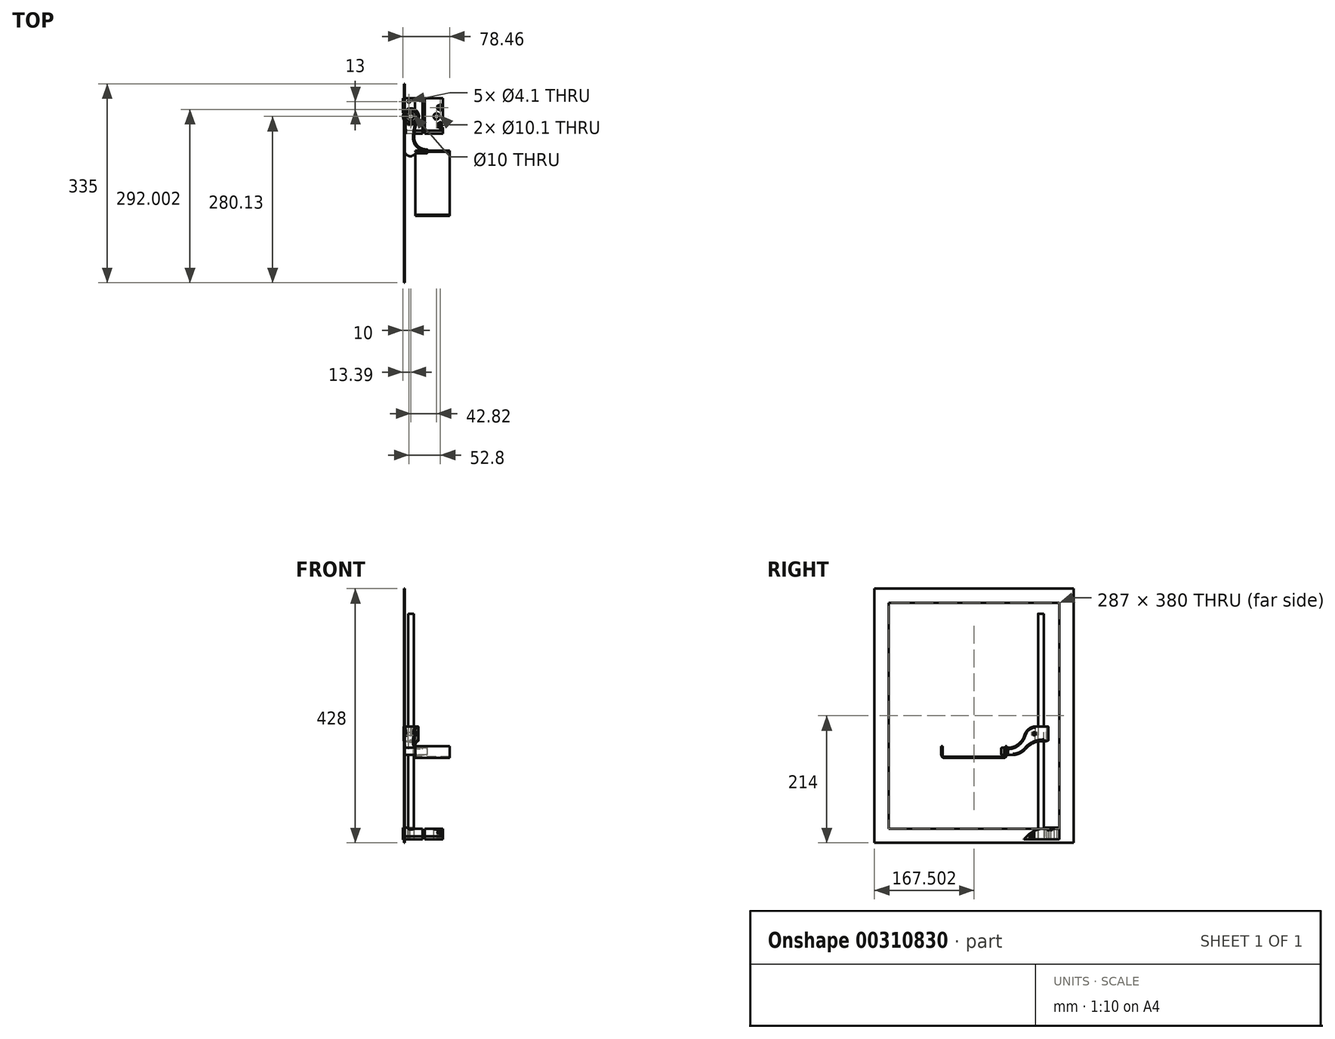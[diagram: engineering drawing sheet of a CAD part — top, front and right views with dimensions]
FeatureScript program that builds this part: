
annotation { "Feature Type Name" : "Feature", "Feature Type Description" : "" }
export const myFeature = defineFeature(function(context is Context, id is Id, definition is map)
    precondition{}
    {
        {
            var Q0;
            Q0=qCreatedBy(makeId("Top.planeOp"),FACE);
            var sketch = newSketch(context, id + "F0", { "sketchPlane" : qUnion([Q0])});
            skLineSegment(sketch, "E0", {"start": v(-50.7, -30.46) * mm, "end": v(-50.7, 5.6) * mm, "construction": true});
            skLineSegment(sketch, "E1", {"start": v(-12.7, -29.55) * mm, "end": v(-12.7, -27.28) * mm});
            skLineSegment(sketch, "E2", {"start": v(-12.7, -27.28) * mm, "end": v(-32.5, -27.28) * mm});
            skLineSegment(sketch, "E3", {"start": v(-32.5, -25.09) * mm, "end": v(-12.7, -25.09) * mm});
            skLineSegment(sketch, "E4", {"start": v(-12.7, -25.09) * mm, "end": v(-12.7, -23) * mm});
            skLineSegment(sketch, "E5", {"start": v(-12.7, -23) * mm, "end": v(-14.49, -23) * mm});
            skLineSegment(sketch, "E6", {"start": v(-34.49, -3) * mm, "end": v(-34.49, -2.73) * mm});
            skLineSegment(sketch, "E7", {"start": v(-32.5, -25.09) * mm, "end": v(-32.5, -27.28) * mm});
            skLineSegment(sketch, "E8", {"start": v(-40, -30.46) * mm, "end": v(-40, 32.54) * mm, "construction": true});
            skArc(sketch, "E9", {"start": v(-41, 41.99) * mm, "mid": v(-40, 23.04) * mm, "end": v(-39, 41.99) * mm});
            skArc(sketch, "E10", {"start": v(-28.44, 27.77) * mm, "mid": v(-29.34, 39.07) * mm, "end": v(-39, 45) * mm});
            skPoint(sketch, "E11.visualSharp", {"position": v(-50.7, 26.08) * mm});
            skArc(sketch, "E11.filletArc", {"start": v(-50.7, 5.6) * mm, "mid": v(-51.12, 18.27) * mm, "end": v(-52.39, 30.88) * mm});
            skPoint(sketch, "E12.visualSharp", {"position": v(-34.49, -23) * mm});
            skArc(sketch, "E12.filletArc", {"start": v(-34.49, -3) * mm, "mid": v(-28.63, -17.14) * mm, "end": v(-14.49, -23) * mm});
            skPoint(sketch, "E13.visualSharp", {"position": v(-34.49, 21.32) * mm});
            skArc(sketch, "E13.filletArc", {"start": v(-28.44, 27.77) * mm, "mid": v(-32.96, 12.82) * mm, "end": v(-34.49, -2.73) * mm});
            skLineSegment(sketch, "E14", {"start": v(-50.7, -24.74) * mm, "end": v(-50.7, 5.6) * mm});
            skLineSegment(sketch, "E15", {"start": v(-29.97, -29.55) * mm, "end": v(-12.7, -29.55) * mm});
            skPoint(sketch, "E16.visualSharp", {"position": v(-50.7, -40.46) * mm});
            skPoint(sketch, "E17.newPointA", {"position": v(-32.5, -24.6) * mm});
            skLineSegment(sketch, "E18.bottom", {"start": v(-39, 40.44) * mm, "end": v(-41, 40.44) * mm, "construction": true});
            skLineSegment(sketch, "E18.top", {"start": v(-39, 48.56) * mm, "end": v(-41, 48.56) * mm, "construction": true});
            skLineSegment(sketch, "E18.left", {"start": v(-39, 40.44) * mm, "end": v(-39, 48.56) * mm, "construction": true});
            skLineSegment(sketch, "E18.right", {"start": v(-41, 40.44) * mm, "end": v(-41, 48.56) * mm, "construction": true});
            skPoint(sketch, "E18.middle", {"position": v(-40, 44.5) * mm});
            skLineSegment(sketch, "E19", {"start": v(-41, 45) * mm, "end": v(-41, 41.99) * mm});
            skPoint(sketch, "E19.endSnap0", {"position": v(-41, 44.5) * mm});
            skLineSegment(sketch, "E20", {"start": v(-39, 45) * mm, "end": v(-39, 41.99) * mm});
            skArc(sketch, "E21.trimOffspring", {"start": v(-41, 45) * mm, "mid": v(-49.73, 40.39) * mm, "end": v(-52.39, 30.88) * mm});
            skLineSegment(sketch, "E22", {"start": v(0, -74.8) * mm, "end": v(0, 75.26) * mm, "construction": true});
            skArc(sketch, "E23.MirrorCS", {"start": v(41, 45) * mm, "mid": v(49.73, 40.39) * mm, "end": v(52.39, 30.88) * mm});
            skLineSegment(sketch, "E24.MirrorCS", {"start": v(41, 45) * mm, "end": v(41, 41.99) * mm});
            skArc(sketch, "E25.MirrorCS", {"start": v(50.7, 5.6) * mm, "mid": v(51.12, 18.27) * mm, "end": v(52.39, 30.88) * mm});
            skLineSegment(sketch, "E26.MirrorCS", {"start": v(12.7, -27.28) * mm, "end": v(32.5, -27.28) * mm});
            skPoint(sketch, "E27.MirrorP", {"position": v(41, 44.5) * mm});
            skLineSegment(sketch, "E28.MirrorCS", {"start": v(34.49, -3) * mm, "end": v(34.49, -2.73) * mm});
            skPoint(sketch, "E29.MirrorP", {"position": v(32.5, -24.6) * mm});
            skPoint(sketch, "E30.MirrorP", {"position": v(50.7, -40.46) * mm});
            skLineSegment(sketch, "E31.MirrorCS", {"start": v(32.5, -29.55) * mm, "end": v(12.7, -29.55) * mm});
            skLineSegment(sketch, "E32.MirrorCS", {"start": v(39, 48.56) * mm, "end": v(41, 48.56) * mm, "construction": true});
            skPoint(sketch, "E33.MirrorP", {"position": v(34.49, -23) * mm});
            skLineSegment(sketch, "E34.MirrorCS", {"start": v(32.5, -25.09) * mm, "end": v(12.7, -25.09) * mm});
            skPoint(sketch, "E35.MirrorP", {"position": v(50.7, 26.08) * mm});
            skLineSegment(sketch, "E36.MirrorCS", {"start": v(32.5, -25.09) * mm, "end": v(32.5, -27.28) * mm});
            skLineSegment(sketch, "E37.MirrorCS", {"start": v(39, 45) * mm, "end": v(39, 41.99) * mm});
            skLineSegment(sketch, "E38.MirrorCS", {"start": v(41, 40.44) * mm, "end": v(41, 48.56) * mm, "construction": true});
            skLineSegment(sketch, "E39.MirrorCS", {"start": v(12.7, -25.09) * mm, "end": v(12.7, -23) * mm});
            skLineSegment(sketch, "E40.MirrorCS", {"start": v(40, -30.46) * mm, "end": v(40, 32.54) * mm, "construction": true});
            skLineSegment(sketch, "E41.MirrorCS", {"start": v(12.7, -29.55) * mm, "end": v(33.16, -29.55) * mm, "construction": true});
            skPoint(sketch, "E42.MirrorP", {"position": v(40, 44.5) * mm});
            skLineSegment(sketch, "E43.MirrorCS", {"start": v(12.7, -23) * mm, "end": v(14.49, -23) * mm});
            skPoint(sketch, "E44.MirrorP", {"position": v(34.49, 21.32) * mm});
            skArc(sketch, "E45.MirrorCS", {"start": v(41, 41.99) * mm, "mid": v(40, 23.04) * mm, "end": v(39, 41.99) * mm});
            skLineSegment(sketch, "E46.MirrorCS", {"start": v(50.7, -30.46) * mm, "end": v(50.7, 5.6) * mm, "construction": true});
            skArc(sketch, "E47.MirrorCS", {"start": v(34.49, -3) * mm, "mid": v(28.63, -17.14) * mm, "end": v(14.49, -23) * mm});
            skLineSegment(sketch, "E48.MirrorCS", {"start": v(39, 40.44) * mm, "end": v(39, 48.56) * mm, "construction": true});
            skLineSegment(sketch, "E49.MirrorCS", {"start": v(39, 40.44) * mm, "end": v(41, 40.44) * mm, "construction": true});
            skLineSegment(sketch, "E50.MirrorCS", {"start": v(50.7, -24.74) * mm, "end": v(50.7, 5.6) * mm});
            skArc(sketch, "E51.MirrorCS", {"start": v(28.44, 27.77) * mm, "mid": v(29.34, 39.07) * mm, "end": v(39, 45) * mm});
            skLineSegment(sketch, "E52.MirrorCS", {"start": v(12.7, -29.55) * mm, "end": v(12.7, -27.28) * mm});
            skArc(sketch, "E53.MirrorCS", {"start": v(28.44, 27.77) * mm, "mid": v(32.96, 12.82) * mm, "end": v(34.49, -2.73) * mm});
            skArc(sketch, "E54", {"start": v(-50.7, -24.74) * mm, "mid": v(-44.43, -33.83) * mm, "end": v(-33.7, -31.22) * mm});
            skPoint(sketch, "E55.visualSharp", {"position": v(-32.5, -29.55) * mm});
            skArc(sketch, "E55.filletArc", {"start": v(-29.97, -29.55) * mm, "mid": v(-32.01, -29.98) * mm, "end": v(-33.7, -31.22) * mm});
            skArc(sketch, "E56.MirrorCS", {"start": v(50.7, -24.74) * mm, "mid": v(44.43, -33.83) * mm, "end": v(33.7, -31.22) * mm});
            skArc(sketch, "E57.MirrorCS", {"start": v(29.97, -29.55) * mm, "mid": v(32.01, -29.98) * mm, "end": v(33.7, -31.22) * mm});
            skLineSegment(sketch, "E58", {"start": v(-59.42, -34.47) * mm, "end": v(64.51, -34.47) * mm, "construction": true});
            skSolve(sketch);
        }
        {
            var Q0;
            Q0=makeQuery(id+"F0.imprint","IMPRINT",FACE,{"disambiguationData":[TD([[makeQuery(id+"F0.imprint","IMPRINT",EDGE,{"derivedFrom":sQuery(id+"F0.wireOp",EDGE,"E1")}),1.0]])]});
            var Q1;
            Q1=makeQuery(id+"F0.imprint","IMPRINT",FACE,{"disambiguationData":[TD([[makeQuery(id+"F0.imprint","IMPRINT",EDGE,{"derivedFrom":sQuery(id+"F0.wireOp",EDGE,"E23.MirrorCS")}),-1.0]])]});
            extrude(context, id + "F1", {"entities" : qUnion([Q0, Q1]), "depth" : 48 * mm});
        }
        {
            var Q0;
            Q0=qCreatedBy(makeId("Right.planeOp"),FACE);
            var sketch = newSketch(context, id + "F2", { "sketchPlane" : qUnion([Q0])});
            skLineSegment(sketch, "E59", {"start": v(-34.5, 0) * mm, "end": v(-34.5, 48) * mm, "construction": true});
            skLineSegment(sketch, "E60", {"start": v(45, 0) * mm, "end": v(45, 48) * mm, "construction": true});
            skLineSegment(sketch, "E61", {"start": v(45, 24) * mm, "end": v(-34.5, 24) * mm, "construction": true});
            skLineSegment(sketch, "E62", {"start": v(20, 0) * mm, "end": v(20, 48) * mm, "construction": true});
            skLineSegment(sketch, "E63", {"start": v(-34.5, 0) * mm, "end": v(-15.8, 0) * mm});
            skLineSegment(sketch, "E64", {"start": v(5.86, 9.24) * mm, "end": v(8.19, 11.67) * mm});
            skLineSegment(sketch, "E65", {"start": v(37.07, 24) * mm, "end": v(45, 24) * mm});
            skPoint(sketch, "E66.visualSharp", {"position": v(20, 24) * mm});
            skArc(sketch, "E66.filletArc", {"start": v(37.07, 24) * mm, "mid": v(21.37, 20.79) * mm, "end": v(8.19, 11.67) * mm});
            skPoint(sketch, "E67.visualSharp", {"position": v(-3, 0) * mm});
            skArc(sketch, "E67.filletArc", {"start": v(-15.8, 0) * mm, "mid": v(-4.03, 2.4) * mm, "end": v(5.86, 9.24) * mm});
            skLineSegment(sketch, "E68", {"start": v(45, 48) * mm, "end": v(24.14, 48) * mm});
            skLineSegment(sketch, "E69", {"start": v(5.28, 34.67) * mm, "end": v(4.34, 32) * mm});
            skLineSegment(sketch, "E70", {"start": v(-23.94, 12) * mm, "end": v(-34.5, 12) * mm});
            skPoint(sketch, "E71.visualSharp", {"position": v(10, 48) * mm});
            skArc(sketch, "E71.filletArc", {"start": v(24.14, 48) * mm, "mid": v(12.6, 44.33) * mm, "end": v(5.28, 34.67) * mm});
            skPoint(sketch, "E72.visualSharp", {"position": v(-2.73, 12) * mm});
            skArc(sketch, "E72.filletArc", {"start": v(-23.94, 12) * mm, "mid": v(-6.63, 17.5) * mm, "end": v(4.34, 32) * mm});
            skLineSegment(sketch, "E73", {"start": v(24.14, 48) * mm, "end": v(-34.5, 48) * mm});
            skLineSegment(sketch, "E74", {"start": v(-34.5, 48) * mm, "end": v(-34.5, 12) * mm});
            skLineSegment(sketch, "E75", {"start": v(45, 24) * mm, "end": v(45, 0) * mm});
            skLineSegment(sketch, "E76", {"start": v(45, 0) * mm, "end": v(-15.8, 0) * mm});
            skSolve(sketch);
        }
        {
            var Q0;
            Q0 = qSketchRegion(id + "F2", true);
            extrude(context, id + "F3", {"entities" : qUnion([Q0]), "operationType" : NewBodyOperationType.REMOVE, "endBound" : BoundingType.THROUGH_ALL, "oppositeDirection" : true, "depth" : 25 * mm, "hasSecondDirection" : true, "secondDirectionBound" : BoundingType.THROUGH_ALL, "secondDirectionOppositeDirection" : false, "secondDirectionDepth" : 25 * mm});
        }
        {
            var Q0;
            Q0=makeQuery(id+"F3.boolean.opBoolean","INTERSECT",EDGE,{"derivedFrom":[makeQuery(id+"F1.opExtrude","SWEPT_FACE",FACE,{"disambiguationData":[OSD([sQuery(id+"F0.wireOp",EDGE,"E56.MirrorCS")])]}),makeQuery(id+"F3.opExtrude","SWEPT_FACE",FACE,{"disambiguationData":[OSD([sQuery(id+"F2.wireOp",EDGE,"E70")])]})]});
            var Q1;
            Q1=makeQuery(id+"F3.boolean.opBoolean","INTERSECT",EDGE,{"derivedFrom":[makeQuery(id+"F1.opExtrude","SWEPT_FACE",FACE,{"disambiguationData":[OSD([sQuery(id+"F0.wireOp",EDGE,"E50.MirrorCS")])]}),makeQuery(id+"F3.opExtrude","SWEPT_FACE",FACE,{"disambiguationData":[OSD([sQuery(id+"F2.wireOp",EDGE,"E67.filletArc")])]})]});
            var Q2;
            Q2=makeQuery(id+"F3.boolean.opBoolean","INTERSECT",EDGE,{"derivedFrom":[makeQuery(id+"F1.opExtrude","SWEPT_FACE",FACE,{"disambiguationData":[OSD([sQuery(id+"F0.wireOp",EDGE,"E14")])]}),makeQuery(id+"F3.opExtrude","SWEPT_FACE",FACE,{"disambiguationData":[OSD([sQuery(id+"F2.wireOp",EDGE,"E72.filletArc")])]})]});
            var Q3;
            Q3=makeQuery(id+"F3.boolean.opBoolean","INTERSECT",EDGE,{"derivedFrom":[makeQuery(id+"F1.opExtrude","SWEPT_FACE",FACE,{"disambiguationData":[OSD([sQuery(id+"F0.wireOp",EDGE,"E14")])]}),makeQuery(id+"F3.opExtrude","SWEPT_FACE",FACE,{"disambiguationData":[OSD([sQuery(id+"F2.wireOp",EDGE,"E67.filletArc")])]})]});
            var Q4;
            Q4=makeQuery(id+"F3.boolean.opBoolean","INTERSECT",EDGE,{"derivedFrom":[makeQuery(id+"F1.opExtrude","SWEPT_FACE",FACE,{"disambiguationData":[OSD([sQuery(id+"F0.wireOp",EDGE,"E53.MirrorCS")])]}),makeQuery(id+"F3.opExtrude","SWEPT_FACE",FACE,{"disambiguationData":[OSD([sQuery(id+"F2.wireOp",EDGE,"E71.filletArc")])]})]});
            var Q5;
            Q5=makeQuery(id+"F3.boolean.opBoolean","INTERSECT",EDGE,{"derivedFrom":[makeQuery(id+"F1.opExtrude","SWEPT_FACE",FACE,{"disambiguationData":[OSD([sQuery(id+"F0.wireOp",EDGE,"E13.filletArc")])]}),makeQuery(id+"F3.opExtrude","SWEPT_FACE",FACE,{"disambiguationData":[OSD([sQuery(id+"F2.wireOp",EDGE,"E71.filletArc")])]})]});
            var Q6;
            Q6=makeQuery(id+"F3.boolean.opBoolean","INTERSECT",EDGE,{"derivedFrom":[makeQuery(id+"F1.opExtrude","SWEPT_FACE",FACE,{"disambiguationData":[OSD([sQuery(id+"F0.wireOp",EDGE,"E13.filletArc")])]}),makeQuery(id+"F3.opExtrude","SWEPT_FACE",FACE,{"disambiguationData":[OSD([sQuery(id+"F2.wireOp",EDGE,"E66.filletArc")])]})]});
            var Q7;
            Q7=makeQuery(id+"F3.boolean.opBoolean","INTERSECT",EDGE,{"derivedFrom":[makeQuery(id+"F1.opExtrude","SWEPT_FACE",FACE,{"disambiguationData":[OSD([sQuery(id+"F0.wireOp",EDGE,"E53.MirrorCS")])]}),makeQuery(id+"F3.opExtrude","SWEPT_FACE",FACE,{"disambiguationData":[OSD([sQuery(id+"F2.wireOp",EDGE,"E66.filletArc")])]})]});
            fillet(context, id + "F4", {"entities" : qUnion([Q0, Q1, Q2, Q3, Q4, Q5, Q6, Q7]), "radius" : 2 * mm, "tangentPropagation" : true, "rho" : .8, "crossSection" : FilletCrossSection.CONIC, "allowEdgeOverflow" : false});
        }
        {
            var Q0;
            Q0=qCreatedBy(makeId("Right.planeOp"),FACE);
            var Q1;
            Q1=sQuery(id+"F0.wireOp",VERTEX,"E10.center");
            cPlane(context, id + "F5", {"entities" : qUnion([Q0, Q1]), "cplaneType" : CPlaneType.PLANE_POINT, "offset" : 25 * mm, "width" : 150 * mm, "height" : 150 * mm});
        }
        {
            var Q0;
            Q0=qCreatedBy(id+"F5.planeOp",FACE);
            var sketch = newSketch(context, id + "F6", { "sketchPlane" : qUnion([Q0])});
            skLineSegment(sketch, "E77", {"start": v(45, 0) * mm, "end": v(45, 48) * mm, "construction": true});
            skLineSegment(sketch, "E78", {"start": v(42, 0) * mm, "end": v(42, 48) * mm, "construction": true});
            skLineSegment(sketch, "E79", {"start": v(32.5, 0) * mm, "end": v(32.5, 48) * mm, "construction": true});
            skLineSegment(sketch, "E80.MirrorCS", {"start": v(23, 0) * mm, "end": v(23, 48) * mm, "construction": true});
            skLineSegment(sketch, "E81.MirrorCS", {"start": v(20, 0) * mm, "end": v(20, 48) * mm, "construction": true});
            skLineSegment(sketch, "E82", {"start": v(45, 24) * mm, "end": v(20, 24) * mm, "construction": true});
            skLineSegment(sketch, "E83", {"start": v(20, 48) * mm, "end": v(45, 48) * mm, "construction": true});
            skLineSegment(sketch, "E84", {"start": v(45, 48) * mm, "end": v(45, 24) * mm, "construction": true});
            skLineSegment(sketch, "E85", {"start": v(45, 36) * mm, "end": v(18, 36) * mm, "construction": true});
            skLineSegment(sketch, "E86.bottom", {"start": v(17, 33.5) * mm, "end": v(19, 33.5) * mm});
            skLineSegment(sketch, "E86.top", {"start": v(17, 38.5) * mm, "end": v(19, 38.5) * mm});
            skLineSegment(sketch, "E86.left", {"start": v(17, 33.5) * mm, "end": v(17, 38.5) * mm});
            skLineSegment(sketch, "E86.right", {"start": v(19, 33.5) * mm, "end": v(19, 38.5) * mm});
            skPoint(sketch, "E86.middle", {"position": v(18, 36) * mm});
            skSolve(sketch);
        }
        {
            var Q0;
            Q0 = qSketchRegion(id + "F6", true);
            var Q1;
            Q1=sQuery(id+"F6.wireOp",EDGE,"E79");
            revolve(context, id + "F7", {"entities" : qUnion([Q0]), "axis" : qUnion([Q1]), "revolveType" : RevolveType.FULL, "oppositeDirection" : true});
        }
        {
            var Q0;
            Q0=makeQuery(id+"F7.opRevolve","SWEPT_BODY",BODY,{"disambiguationData":[OSD([sQuery(id+"F6.wireOp",EDGE,"E86.bottom"),sQuery(id+"F6.wireOp",EDGE,"E86.top"),sQuery(id+"F6.wireOp",EDGE,"E86.left"),sQuery(id+"F6.wireOp",EDGE,"E86.right")])]});
            var Q1;
            Q1=qCreatedBy(makeId("Right.planeOp"),FACE);
            mirror(context, id + "F8", {"entities" : qUnion([Q0]), "mirrorPlane" : qUnion([Q1])});
        }
        {
            var Q0;
            Q0=makeQuery(id+"F7.opRevolve","SWEPT_BODY",BODY,{"disambiguationData":[OSD([sQuery(id+"F6.wireOp",EDGE,"E86.bottom"),sQuery(id+"F6.wireOp",EDGE,"E86.top"),sQuery(id+"F6.wireOp",EDGE,"E86.left"),sQuery(id+"F6.wireOp",EDGE,"E86.right")])]});
            var Q1;
            Q1=makeQuery(id+"F8.opPattern","COPY",BODY,{"derivedFrom":makeQuery(id+"F7.opRevolve","SWEPT_BODY",BODY,{"disambiguationData":[OSD([sQuery(id+"F6.wireOp",EDGE,"E86.bottom"),sQuery(id+"F6.wireOp",EDGE,"E86.top"),sQuery(id+"F6.wireOp",EDGE,"E86.left"),sQuery(id+"F6.wireOp",EDGE,"E86.right")])]}),"instanceName":"1"});
            var Q2;
            Q2=makeQuery(id+"F1.opExtrude","SWEPT_BODY",BODY,{"disambiguationData":[OSD([sQuery(id+"F0.wireOp",EDGE,"E1"),sQuery(id+"F0.wireOp",EDGE,"E2"),sQuery(id+"F0.wireOp",EDGE,"E3"),sQuery(id+"F0.wireOp",EDGE,"E4"),sQuery(id+"F0.wireOp",EDGE,"E5"),sQuery(id+"F0.wireOp",EDGE,"E6"),sQuery(id+"F0.wireOp",EDGE,"E7"),sQuery(id+"F0.wireOp",EDGE,"E9"),sQuery(id+"F0.wireOp",EDGE,"E10"),sQuery(id+"F0.wireOp",EDGE,"E11.filletArc"),sQuery(id+"F0.wireOp",EDGE,"E12.filletArc"),sQuery(id+"F0.wireOp",EDGE,"E13.filletArc"),sQuery(id+"F0.wireOp",EDGE,"E14"),sQuery(id+"F0.wireOp",EDGE,"E15"),sQuery(id+"F0.wireOp",EDGE,"E19"),sQuery(id+"F0.wireOp",EDGE,"E20"),sQuery(id+"F0.wireOp",EDGE,"E21.trimOffspring"),sQuery(id+"F0.wireOp",EDGE,"E54"),sQuery(id+"F0.wireOp",EDGE,"E55.filletArc")])]});
            var Q3;
            Q3=makeQuery(id+"F1.opExtrude","SWEPT_BODY",BODY,{"disambiguationData":[OSD([sQuery(id+"F0.wireOp",EDGE,"E23.MirrorCS"),sQuery(id+"F0.wireOp",EDGE,"E24.MirrorCS"),sQuery(id+"F0.wireOp",EDGE,"E25.MirrorCS"),sQuery(id+"F0.wireOp",EDGE,"E26.MirrorCS"),sQuery(id+"F0.wireOp",EDGE,"E28.MirrorCS"),sQuery(id+"F0.wireOp",EDGE,"E31.MirrorCS"),sQuery(id+"F0.wireOp",EDGE,"E34.MirrorCS"),sQuery(id+"F0.wireOp",EDGE,"E36.MirrorCS"),sQuery(id+"F0.wireOp",EDGE,"E37.MirrorCS"),sQuery(id+"F0.wireOp",EDGE,"E39.MirrorCS"),sQuery(id+"F0.wireOp",EDGE,"E43.MirrorCS"),sQuery(id+"F0.wireOp",EDGE,"E45.MirrorCS"),sQuery(id+"F0.wireOp",EDGE,"E47.MirrorCS"),sQuery(id+"F0.wireOp",EDGE,"E50.MirrorCS"),sQuery(id+"F0.wireOp",EDGE,"E51.MirrorCS"),sQuery(id+"F0.wireOp",EDGE,"E52.MirrorCS"),sQuery(id+"F0.wireOp",EDGE,"E53.MirrorCS"),sQuery(id+"F0.wireOp",EDGE,"E56.MirrorCS"),sQuery(id+"F0.wireOp",EDGE,"E57.MirrorCS")])]});
            booleanBodies(context, id + "F9", {"operationType" : BooleanOperationType.SUBTRACTION, "tools" : qUnion([Q0, Q1]), "targets" : qUnion([Q2, Q3])});
        }
        {
            var Q0;
            Q0=makeQuery(id+"F1.opExtrude","SWEPT_FACE",FACE,{"disambiguationData":[OSD([sQuery(id+"F0.wireOp",EDGE,"E7")])]});
            var sketch = newSketch(context, id + "F10", { "sketchPlane" : qUnion([Q0])});
            skLineSegment(sketch, "E87.bottom", {"start": v(-25.09, 15) * mm, "end": v(-135.09, 15) * mm, "construction": true});
            skLineSegment(sketch, "E87.top", {"start": v(-30.09, -5) * mm, "end": v(-130.09, -5) * mm});
            skLineSegment(sketch, "E87.left", {"start": v(-25.09, 15) * mm, "end": v(-25.09, 0) * mm});
            skLineSegment(sketch, "E87.right", {"start": v(-135.09, 15) * mm, "end": v(-135.09, 0) * mm});
            skPoint(sketch, "E88.visualSharp", {"position": v(-25.09, -5) * mm});
            skArc(sketch, "E88.filletArc", {"start": v(-30.09, -5) * mm, "mid": v(-26.55, -3.54) * mm, "end": v(-25.09, 0) * mm});
            skPoint(sketch, "E89.visualSharp", {"position": v(-135.09, -5) * mm});
            skArc(sketch, "E89.filletArc", {"start": v(-135.09, 0) * mm, "mid": v(-133.62, -3.54) * mm, "end": v(-130.09, -5) * mm});
            skLineSegment(sketch, "E90.0", {"start": v(-133.09, 15) * mm, "end": v(-133.09, 0) * mm});
            skLineSegment(sketch, "E90.1", {"start": v(-27.09, 15) * mm, "end": v(-27.09, 0) * mm});
            skArc(sketch, "E90.2", {"start": v(-30.09, -3) * mm, "mid": v(-27.97, -2.12) * mm, "end": v(-27.09, 0) * mm});
            skLineSegment(sketch, "E90.3", {"start": v(-30.09, -3) * mm, "end": v(-130.09, -3) * mm});
            skArc(sketch, "E90.4", {"start": v(-133.09, 0) * mm, "mid": v(-132.2, -2.12) * mm, "end": v(-130.09, -3) * mm});
            skLineSegment(sketch, "E91", {"start": v(-25.09, 15) * mm, "end": v(-27.09, 15) * mm});
            skLineSegment(sketch, "E92", {"start": v(-133.09, 15) * mm, "end": v(-135.09, 15) * mm});
            skSolve(sketch);
        }
        {
            var Q0;
            Q0 = qSketchRegion(id + "F10", true);
            extrude(context, id + "F11", {"entities" : qUnion([Q0]), "depth" : 57.57 * mm});
        }
        {
            var Q0;
            Q0=qCreatedBy(makeId("Top.planeOp"),FACE);
            var Q1;
            Q1=makeQuery(id+"F1.opExtrude","CAP_VERTEX",VERTEX,{"disambiguationData":[OSD([sQuery(id+"F0.wireOp",EDGE,"E9"),sQuery(id+"F0.wireOp",EDGE,"E19")])],"isStart":false});
            cPlane(context, id + "F12", {"entities" : qUnion([Q0, Q1]), "cplaneType" : CPlaneType.PLANE_POINT, "offset" : 25 * mm, "width" : 150 * mm, "height" : 150 * mm});
        }
        {
            var Q0;
            Q0=qCreatedBy(id+"F12.planeOp",FACE);
            var sketch = newSketch(context, id + "F13", { "sketchPlane" : qUnion([Q0])});
            skCircle(sketch, "E93", {"center": v(-40, 32.54) * mm, "radius": 9.5 * mm});
            skCircle(sketch, "E94", {"center": v(-40, 32.54) * mm, "radius": 5 * mm});
            skSolve(sketch);
        }
        {
            var Q0;
            Q0 = qSketchRegion(id + "F13", true);
            extrude(context, id + "F14", {"entities" : qUnion([Q0]), "oppositeDirection" : true, "depth" : 25 * mm});
        }
        {
            var Q0;
            Q0=makeQuery(id+"F14.opExtrude","CAP_FACE",FACE,{"disambiguationData":[OSD([sQuery(id+"F13.wireOp",EDGE,"E93"),sQuery(id+"F13.wireOp",EDGE,"E94")])],"isStart":true});
            var sketch = newSketch(context, id + "F15", { "sketchPlane" : qUnion([Q0])});
            skCircle(sketch, "E95", {"center": v(-40, 32.54) * mm, "radius": 5 * mm});
            skSolve(sketch);
        }
        {
            var Q0;
            Q0 = qSketchRegion(id + "F15", true);
            extrude(context, id + "F16", {"entities" : qUnion([Q0]), "depth" : 190 * mm, "hasSecondDirection" : true, "secondDirectionOppositeDirection" : true, "secondDirectionDepth" : 190 * mm});
        }
        {
            var Q0;
            Q0=makeQuery(id+"F16.opExtrude","CAP_FACE",FACE,{"disambiguationData":[OSD([sQuery(id+"F15.wireOp",EDGE,"E95")])],"isStart":true});
            var sketch = newSketch(context, id + "F17", { "sketchPlane" : qUnion([Q0])});
            skCircle(sketch, "E96", {"center": v(-40, -32.54) * mm, "radius": 5.05 * mm});
            skLineSegment(sketch, "E97.bottom", {"start": v(-50.6, -63.41) * mm, "end": v(-20.6, -63.41) * mm});
            skLineSegment(sketch, "E97.top", {"start": v(-50.6, -1.67) * mm, "end": v(-20.6, -1.67) * mm});
            skLineSegment(sketch, "E97.left", {"start": v(-50.59, -63.41) * mm, "end": v(-50.6, -1.67) * mm});
            skLineSegment(sketch, "E97.right", {"start": v(-20.6, -63.41) * mm, "end": v(-20.6, -1.67) * mm});
            skPoint(sketch, "E97.middle", {"position": v(-35.6, -32.54) * mm});
            skLineSegment(sketch, "E98", {"start": v(-40, -1.67) * mm, "end": v(-40, -63.41) * mm, "construction": true});
            skSolve(sketch);
        }
        {
            var Q0;
            Q0 = qSketchRegion(id + "F17", true);
            extrude(context, id + "F18", {"entities" : qUnion([Q0]), "oppositeDirection" : true, "depth" : 18 * mm});
        }
        {
            var Q0;
            Q0=makeQuery(id+"F18.opExtrude","SWEPT_FACE",FACE,{"disambiguationData":[OSD([sQuery(id+"F17.wireOp",EDGE,"E97.left")])]});
            var sketch = newSketch(context, id + "F19", { "sketchPlane" : qUnion([Q0])});
            skLineSegment(sketch, "E99.bottom", {"start": v(-63.41, -124) * mm, "end": v(223.59, -124) * mm});
            skLineSegment(sketch, "E99.top", {"start": v(-63.41, 256) * mm, "end": v(223.59, 256) * mm});
            skLineSegment(sketch, "E99.left", {"start": v(-63.41, -124) * mm, "end": v(-63.41, 256) * mm});
            skLineSegment(sketch, "E99.right", {"start": v(223.59, -124) * mm, "end": v(223.59, 256) * mm});
            skLineSegment(sketch, "E100", {"start": v(80.09, 256) * mm, "end": v(80.09, -124) * mm, "construction": true});
            skLineSegment(sketch, "E101", {"start": v(30.09, -5) * mm, "end": v(130.09, -5) * mm, "construction": true});
            skPoint(sketch, "E102", {"position": v(80.09, -5) * mm});
            skLineSegment(sketch, "E103.0", {"start": v(-87.41, -148) * mm, "end": v(-87.41, 280) * mm});
            skLineSegment(sketch, "E103.1", {"start": v(-87.41, -148) * mm, "end": v(247.59, -148) * mm});
            skLineSegment(sketch, "E103.2", {"start": v(247.59, -148) * mm, "end": v(247.59, 280) * mm});
            skLineSegment(sketch, "E103.3", {"start": v(-87.41, 280) * mm, "end": v(247.59, 280) * mm});
            skSolve(sketch);
        }
        {
            var Q0;
            Q0 = qSketchRegion(id + "F19", true);
            extrude(context, id + "F20", {"entities" : qUnion([Q0]), "depth" : 1.2 * mm});
        }
        {
            var Q0;
            Q0=makeQuery(id+"F18.opExtrude","SWEPT_FACE",FACE,{"disambiguationData":[OSD([sQuery(id+"F17.wireOp",EDGE,"E97.right")])]});
            cPlane(context, id + "F21", {"entities" : qUnion([Q0]), "cplaneType" : CPlaneType.OFFSET, "offset" : 2 * mm, "width" : 150 * mm, "height" : 150 * mm});
        }
        {
            var Q0;
            Q0=makeQuery(id+"F18.opExtrude","SWEPT_BODY",BODY,{"disambiguationData":[OSD([sQuery(id+"F17.wireOp",EDGE,"E96"),sQuery(id+"F17.wireOp",EDGE,"E97.bottom"),sQuery(id+"F17.wireOp",EDGE,"E97.top"),sQuery(id+"F17.wireOp",EDGE,"E97.left"),sQuery(id+"F17.wireOp",EDGE,"E97.right")])]});
            var Q1;
            Q1=qCreatedBy(id+"F21.planeOp",FACE);
            mirror(context, id + "F22", {"entities" : qUnion([Q0]), "mirrorPlane" : qUnion([Q1])});
        }
        {
            var Q0;
            Q0=makeQuery(id+"F18.opExtrude","SWEPT_FACE",FACE,{"disambiguationData":[OSD([sQuery(id+"F17.wireOp",EDGE,"E97.left")])]});
            var sketch = newSketch(context, id + "F23", { "sketchPlane" : qUnion([Q0])});
            skLineSegment(sketch, "E104", {"start": v(-44.58, -124) * mm, "end": v(-38.31, -124) * mm});
            skLineSegment(sketch, "E105", {"start": v(-8.57, -137.2) * mm, "end": v(-7.59, -138.4) * mm});
            skLineSegment(sketch, "E106", {"start": v(14.47, -148) * mm, "end": v(34.92, -148) * mm, "construction": true});
            skLineSegment(sketch, "E107", {"start": v(-19.58, -124) * mm, "end": v(-19.58, -148) * mm, "construction": true});
            skPoint(sketch, "E108.visualSharp", {"position": v(-19.58, -124) * mm});
            skArc(sketch, "E108.filletArc", {"start": v(-7.59, -138.4) * mm, "mid": v(-21.35, -127.78) * mm, "end": v(-38.31, -124) * mm});
            skPoint(sketch, "E109.visualSharp", {"position": v(0.42, -148) * mm});
            skArc(sketch, "E109.filletArc", {"start": v(-8.57, -137.2) * mm, "mid": v(1.75, -145.17) * mm, "end": v(14.47, -148) * mm});
            skLineSegment(sketch, "E110", {"start": v(-44.58, -124) * mm, "end": v(14.47, -124) * mm});
            skLineSegment(sketch, "E111", {"start": v(14.47, -124) * mm, "end": v(14.47, -148) * mm});
            skSolve(sketch);
        }
        {
            var Q0;
            Q0 = qSketchRegion(id + "F23", true);
            extrude(context, id + "F24", {"entities" : qUnion([Q0]), "operationType" : NewBodyOperationType.REMOVE, "endBound" : BoundingType.THROUGH_ALL, "oppositeDirection" : true, "depth" : 25 * mm});
        }
        {
            var Q0;
            Q0=makeQuery(id+"F18.opExtrude","SWEPT_FACE",FACE,{"disambiguationData":[OSD([sQuery(id+"F17.wireOp",EDGE,"E97.bottom")])]});
            var sketch = newSketch(context, id + "F25", { "sketchPlane" : qUnion([Q0])});
            skLineSegment(sketch, "E112", {"start": v(52, -124) * mm, "end": v(33.4, -124) * mm});
            skLineSegment(sketch, "E113", {"start": v(33.4, -124) * mm, "end": v(33.4, -122.6) * mm});
            skLineSegment(sketch, "E114", {"start": v(33.4, -122.6) * mm, "end": v(53.4, -122.6) * mm});
            skLineSegment(sketch, "E115", {"start": v(53.4, -122.6) * mm, "end": v(53.4, -142.6) * mm});
            skLineSegment(sketch, "E116", {"start": v(53.4, -142.6) * mm, "end": v(52, -142.6) * mm});
            skLineSegment(sketch, "E117", {"start": v(52, -142.6) * mm, "end": v(52, -124) * mm});
            skSolve(sketch);
        }
        {
            var Q0;
            Q0 = qSketchRegion(id + "F25", true);
            extrude(context, id + "F26", {"entities" : qUnion([Q0]), "oppositeDirection" : true, "depth" : 25 * mm});
        }
        {
            var Q0;
            Q0=makeQuery(id+"F26.opExtrude","SWEPT_FACE",FACE,{"disambiguationData":[OSD([sQuery(id+"F25.wireOp",EDGE,"E114")])]});
            var sketch = newSketch(context, id + "F27", { "sketchPlane" : qUnion([Q0])});
            skLineSegment(sketch, "E118", {"start": v(-43.4, 38.41) * mm, "end": v(-43.4, 63.41) * mm, "construction": true});
            skPoint(sketch, "E119", {"position": v(-43.4, 50.91) * mm});
            skLineSegment(sketch, "E120", {"start": v(-43.4, 44.41) * mm, "end": v(-43.4, 57.41) * mm});
            skCircle(sketch, "E121", {"center": v(-43.4, 44.41) * mm, "radius": 2.05 * mm});
            skCircle(sketch, "E122", {"center": v(-43.4, 57.41) * mm, "radius": 2.05 * mm});
            skSolve(sketch);
        }
        {
            var Q0;
            Q0=makeQuery(id+"F27.imprint","IMPRINT",FACE,{"disambiguationData":[TD([[makeQuery(id+"F27.imprint","IMPRINT",EDGE,{"derivedFrom":sQuery(id+"F27.wireOp",EDGE,"E122")}),1.0]])]});
            var Q1;
            Q1=makeQuery(id+"F27.imprint","IMPRINT",FACE,{"disambiguationData":[TD([[makeQuery(id+"F27.imprint","IMPRINT",EDGE,{"derivedFrom":sQuery(id+"F27.wireOp",EDGE,"E121")}),1.0]])]});
            extrude(context, id + "F28", {"entities" : qUnion([Q0, Q1]), "operationType" : NewBodyOperationType.REMOVE, "oppositeDirection" : true, "depth" : 25 * mm});
        }
        {
            var Q0;
            Q0=makeQuery(id+"F22.opPattern","COPY",FACE,{"derivedFrom":makeQuery(id+"F18.opExtrude","CAP_FACE",FACE,{"disambiguationData":[OSD([sQuery(id+"F17.wireOp",EDGE,"E96"),sQuery(id+"F17.wireOp",EDGE,"E97.bottom"),sQuery(id+"F17.wireOp",EDGE,"E97.top"),sQuery(id+"F17.wireOp",EDGE,"E97.left"),sQuery(id+"F17.wireOp",EDGE,"E97.right")])],"isStart":false}),"instanceName":"1"});
            var sketch = newSketch(context, id + "F29", { "sketchPlane" : qUnion([Q0])});
            skLineSegment(sketch, "E123", {"start": v(9.4, 47.54) * mm, "end": v(9.4, 17.54) * mm, "construction": true});
            skPoint(sketch, "E124", {"position": v(9.4, 32.54) * mm});
            skCircle(sketch, "E125", {"center": v(9.4, 47.54) * mm, "radius": 2.05 * mm});
            skCircle(sketch, "E126", {"center": v(9.4, 17.54) * mm, "radius": 2.05 * mm});
            skCircle(sketch, "E127.cCircle", {"center": v(9.4, 47.54) * mm, "radius": 3.45 * mm, "construction": true});
            skLineSegment(sketch, "E127.0", {"start": v(5.96, 47.05) * mm, "end": v(5.96, 48.03) * mm});
            skLineSegment(sketch, "E127.1", {"start": v(7.26, 50.28) * mm, "end": v(8.11, 50.77) * mm});
            skLineSegment(sketch, "E127.2", {"start": v(10.7, 50.77) * mm, "end": v(11.56, 50.28) * mm});
            skLineSegment(sketch, "E127.3", {"start": v(12.86, 48.03) * mm, "end": v(12.86, 47.05) * mm});
            skLineSegment(sketch, "E127.4", {"start": v(11.56, 44.8) * mm, "end": v(10.7, 44.3) * mm});
            skLineSegment(sketch, "E127.5", {"start": v(8.11, 44.3) * mm, "end": v(7.26, 44.8) * mm});
            skPoint(sketch, "E127.0.midPoint", {"position": v(5.96, 47.54) * mm});
            skArc(sketch, "E128", {"start": v(10.7, 50.77) * mm, "mid": v(9.4, 53.02) * mm, "end": v(8.11, 50.77) * mm});
            skArc(sketch, "E129.1.0", {"start": v(7.26, 50.28) * mm, "mid": v(4.66, 50.28) * mm, "end": v(5.96, 48.03) * mm});
            skArc(sketch, "E129.2.0", {"start": v(5.96, 47.05) * mm, "mid": v(4.66, 44.8) * mm, "end": v(7.26, 44.8) * mm});
            skArc(sketch, "E129.3.0", {"start": v(8.11, 44.3) * mm, "mid": v(9.4, 42.06) * mm, "end": v(10.7, 44.3) * mm});
            skArc(sketch, "E129.4.0", {"start": v(11.56, 44.8) * mm, "mid": v(14.16, 44.8) * mm, "end": v(12.86, 47.05) * mm});
            skArc(sketch, "E129.5.0", {"start": v(12.86, 48.03) * mm, "mid": v(14.16, 50.28) * mm, "end": v(11.56, 50.28) * mm});
            skLineSegment(sketch, "E130", {"start": v(9.4, 32.54) * mm, "end": v(23.54, 32.54) * mm, "construction": true});
            skLineSegment(sketch, "E131.MirrorCS", {"start": v(10.7, 14.3) * mm, "end": v(11.56, 14.8) * mm});
            skLineSegment(sketch, "E132.MirrorCS", {"start": v(7.26, 14.8) * mm, "end": v(8.11, 14.3) * mm});
            skLineSegment(sketch, "E133.MirrorCS", {"start": v(5.96, 18.03) * mm, "end": v(5.96, 17.05) * mm});
            skLineSegment(sketch, "E134.MirrorCS", {"start": v(12.86, 17.05) * mm, "end": v(12.86, 18.03) * mm});
            skCircle(sketch, "E135.MirrorC", {"center": v(9.4, 17.54) * mm, "radius": 3.45 * mm, "construction": true});
            skLineSegment(sketch, "E136.MirrorCS", {"start": v(8.11, 20.77) * mm, "end": v(7.26, 20.28) * mm});
            skLineSegment(sketch, "E137.MirrorCS", {"start": v(11.56, 20.28) * mm, "end": v(10.7, 20.77) * mm});
            skArc(sketch, "E138.MirrorCS", {"start": v(12.86, 17.05) * mm, "mid": v(14.16, 14.8) * mm, "end": v(11.56, 14.8) * mm});
            skPoint(sketch, "E139.MirrorP", {"position": v(5.96, 17.54) * mm});
            skPoint(sketch, "E140.MirrorP", {"position": v(9.4, 21.52) * mm});
            skArc(sketch, "E141.MirrorCS", {"start": v(10.7, 14.3) * mm, "mid": v(9.4, 12.06) * mm, "end": v(8.11, 14.3) * mm});
            skArc(sketch, "E142.MirrorCS", {"start": v(11.56, 20.28) * mm, "mid": v(14.16, 20.28) * mm, "end": v(12.86, 18.03) * mm});
            skArc(sketch, "E143.MirrorCS", {"start": v(5.96, 18.03) * mm, "mid": v(4.66, 20.28) * mm, "end": v(7.26, 20.28) * mm});
            skPoint(sketch, "E144.MirrorP", {"position": v(5.96, 15.55) * mm});
            skArc(sketch, "E145.MirrorCS", {"start": v(8.11, 20.77) * mm, "mid": v(9.4, 23.02) * mm, "end": v(10.7, 20.77) * mm});
            skArc(sketch, "E146.MirrorCS", {"start": v(7.26, 14.8) * mm, "mid": v(4.66, 14.8) * mm, "end": v(5.96, 17.05) * mm});
            skSolve(sketch);
        }
        {
            var Q0;
            Q0=makeQuery(id+"F29.imprint","IMPRINT",FACE,{"disambiguationData":[TD([[makeQuery(id+"F29.imprint","IMPRINT",EDGE,{"derivedFrom":sQuery(id+"F29.wireOp",EDGE,"E125")}),1.0]])]});
            var Q1;
            Q1=makeQuery(id+"F29.imprint","IMPRINT",FACE,{"disambiguationData":[TD([[makeQuery(id+"F29.imprint","IMPRINT",EDGE,{"derivedFrom":sQuery(id+"F29.wireOp",EDGE,"E126")}),-1.0]])]});
            extrude(context, id + "F30", {"entities" : qUnion([Q0, Q1]), "operationType" : NewBodyOperationType.REMOVE, "endBound" : BoundingType.THROUGH_ALL, "oppositeDirection" : true, "depth" : 25 * mm});
        }
        {
            var Q0;
            Q0=makeQuery(id+"F29.imprint","IMPRINT",FACE,{"disambiguationData":[TD([[makeQuery(id+"F29.imprint","IMPRINT",EDGE,{"derivedFrom":sQuery(id+"F29.wireOp",EDGE,"E125")}),-1.0]])]});
            var Q1;
            {var subQ1=sQuery(id+"F29.wireOp",EDGE,"E131.MirrorCS");Q1=makeQuery(id+"F29.imprint","IMPRINT",FACE,{"disambiguationData":[TD([[makeQuery(id+"F29.imprint","IMPRINT",EDGE,{"derivedFrom":subQ1}),1.0]])]});}
            extrude(context, id + "F31", {"entities" : qUnion([Q0, Q1]), "operationType" : NewBodyOperationType.REMOVE, "oppositeDirection" : true, "depth" : 3 * mm});
        }
    });
